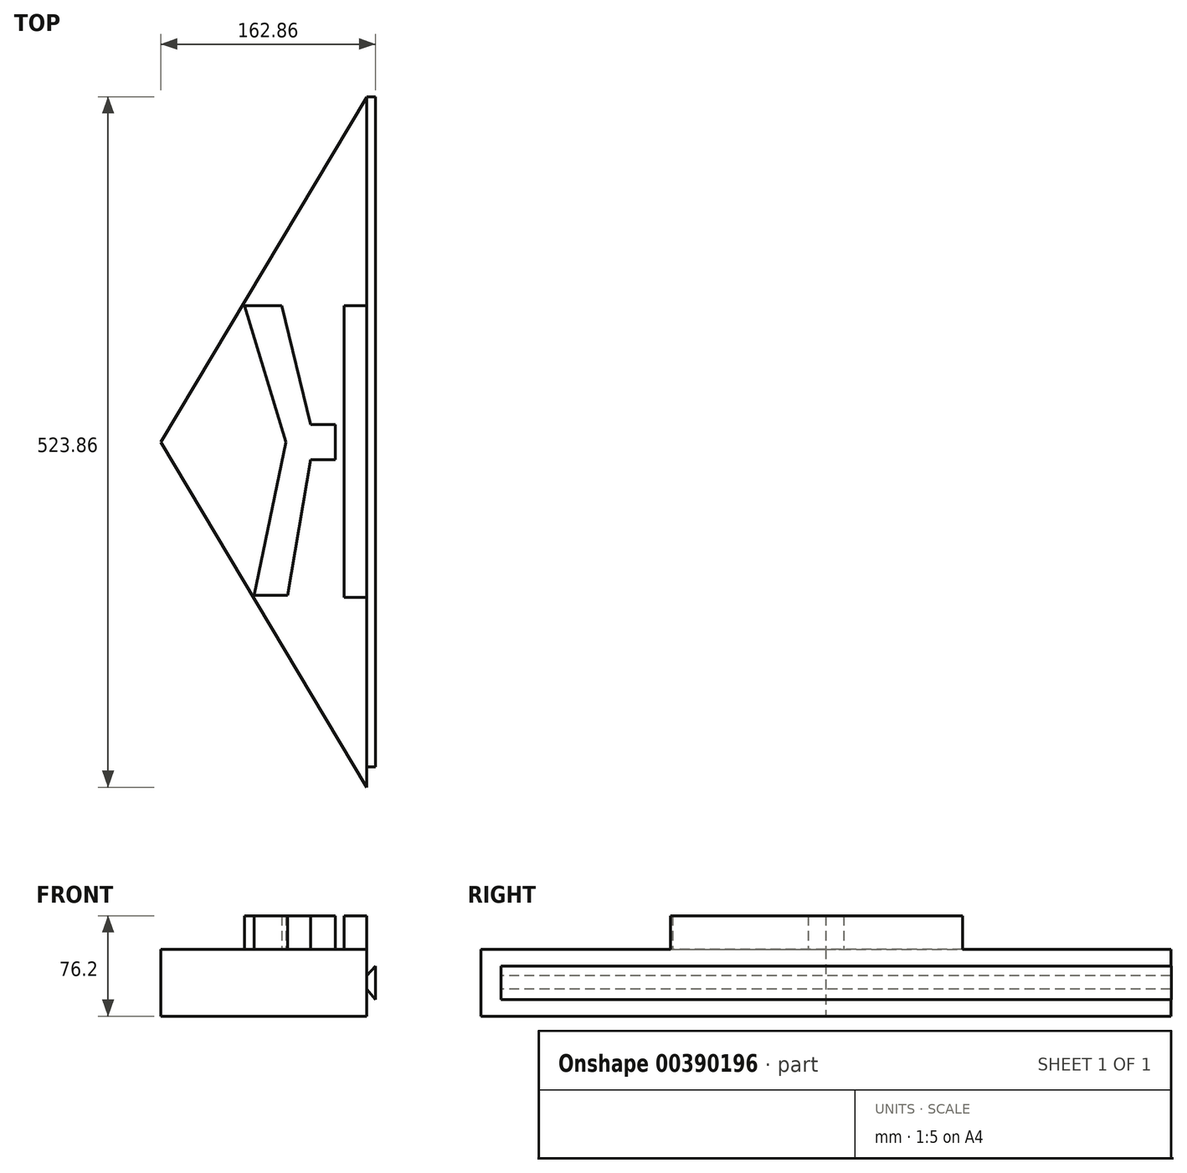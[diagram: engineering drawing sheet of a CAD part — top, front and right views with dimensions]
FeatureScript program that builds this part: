
annotation { "Feature Type Name" : "Feature", "Feature Type Description" : "" }
export const myFeature = defineFeature(function(context is Context, id is Id, definition is map)
    precondition{}
    {
        {
            var Q0;
            Q0=qCreatedBy(makeId("Top.planeOp"),FACE);
            var sketch = newSketch(context, id + "F0", { "sketchPlane" : qUnion([Q0])});
            skLineSegment(sketch, "E0", {"start": v(0, 261.73) * mm, "end": v(0, -261.73) * mm});
            skLineSegment(sketch, "E1", {"start": v(0, -261.73) * mm, "end": v(-156.2, 0) * mm});
            skLineSegment(sketch, "E2", {"start": v(-156.2, 0) * mm, "end": v(0, 261.73) * mm});
            skSolve(sketch);
        }
        {
            var Q0;
            Q0=makeQuery(id+"F0.imprint","IMPRINT",FACE,{"disambiguationData":[TD([[makeQuery(id+"F0.imprint","IMPRINT",EDGE,{"derivedFrom":sQuery(id+"F0.wireOp",EDGE,"E0")}),-1.0]])]});
            extrude(context, id + "F1", {"entities" : qUnion([Q0]), "depth" : 50.8 * mm});
        }
        {
            var Q0;
            Q0=makeQuery(id+"F1.opExtrude","CAP_FACE",FACE,{"disambiguationData":[OSD([sQuery(id+"F0.wireOp",EDGE,"E0"),sQuery(id+"F0.wireOp",EDGE,"E1"),sQuery(id+"F0.wireOp",EDGE,"E2")])],"isStart":false});
            cPlane(context, id + "F2", {"entities" : qUnion([Q0]), "cplaneType" : CPlaneType.OFFSET, "offset" : 0 * mm, "width" : 152.4 * mm, "height" : 152.4 * mm});
        }
        {
            var Q0;
            Q0=qCreatedBy(id+"F2.planeOp",FACE);
            var sketch = newSketch(context, id + "F3", { "sketchPlane" : qUnion([Q0])});
            skLineSegment(sketch, "E3.bottom", {"start": v(0, 103.6) * mm, "end": v(-17.09, 103.6) * mm});
            skLineSegment(sketch, "E3.top", {"start": v(0, -117.89) * mm, "end": v(-17.09, -117.89) * mm});
            skLineSegment(sketch, "E3.left", {"start": v(0, 103.6) * mm, "end": v(0, -117.89) * mm});
            skLineSegment(sketch, "E3.right", {"start": v(-17.09, 103.6) * mm, "end": v(-17.09, -117.89) * mm});
            skLineSegment(sketch, "E4.bottom", {"start": v(-23.86, -13.4) * mm, "end": v(-61.21, -13.4) * mm});
            skLineSegment(sketch, "E4.top", {"start": v(-23.86, 13.4) * mm, "end": v(-61.21, 13.4) * mm});
            skLineSegment(sketch, "E4.left", {"start": v(-23.86, -13.4) * mm, "end": v(-23.86, 13.4) * mm});
            skLineSegment(sketch, "E4.right", {"start": v(-61.21, -13.4) * mm, "end": v(-61.21, 13.4) * mm});
            skPoint(sketch, "E4.middle", {"position": v(-42.54, 0) * mm});
            skLineSegment(sketch, "E5", {"start": v(-61.21, 0) * mm, "end": v(-85.25, -116.21) * mm});
            skLineSegment(sketch, "E6", {"start": v(-85.25, -116.21) * mm, "end": v(-60, -116.21) * mm});
            skLineSegment(sketch, "E7", {"start": v(-60, -116.21) * mm, "end": v(-42.54, -13.4) * mm});
            skLineSegment(sketch, "E8", {"start": v(-61.21, 0) * mm, "end": v(-92.8, 103.65) * mm});
            skLineSegment(sketch, "E9", {"start": v(-92.8, 103.65) * mm, "end": v(-64.5, 103.65) * mm});
            skLineSegment(sketch, "E10", {"start": v(-64.5, 103.65) * mm, "end": v(-42.54, 13.4) * mm});
            skSolve(sketch);
        }
        {
            var Q0;
            Q0 = qSketchRegion(id + "F3", true);
            extrude(context, id + "F4", {"entities" : qUnion([Q0]), "operationType" : NewBodyOperationType.ADD, "depth" : 25.4 * mm});
        }
        {
            var Q0;
            Q0=qCreatedBy(makeId("Front.planeOp"),FACE);
            cPlane(context, id + "F5", {"entities" : qUnion([Q0]), "cplaneType" : CPlaneType.OFFSET, "offset" : 162.56 * mm, "width" : 152.4 * mm, "height" : 152.4 * mm});
        }
        {
            var Q0;
            Q0=qCreatedBy(id+"F5.planeOp",FACE);
            cPlane(context, id + "F6", {"entities" : qUnion([Q0]), "cplaneType" : CPlaneType.OFFSET, "offset" : 83.82 * mm, "width" : 152.4 * mm, "height" : 152.4 * mm});
        }
        {
            var Q0;
            Q0=qCreatedBy(id+"F6.planeOp",FACE);
            var sketch = newSketch(context, id + "F7", { "sketchPlane" : qUnion([Q0])});
            skLineSegment(sketch, "E11", {"start": v(0, 20.42) * mm, "end": v(6.66, 12.72) * mm});
            skLineSegment(sketch, "E12", {"start": v(6.66, 12.72) * mm, "end": v(6.66, 38.05) * mm});
            skLineSegment(sketch, "E13", {"start": v(6.66, 38.05) * mm, "end": v(0, 30.59) * mm});
            skLineSegment(sketch, "E14", {"start": v(0, 30.59) * mm, "end": v(0, 20.42) * mm});
            skSolve(sketch);
        }
        {
            var Q0;
            Q0 = qSketchRegion(id + "F7", true);
            extrude(context, id + "F8", {"entities" : qUnion([Q0]), "operationType" : NewBodyOperationType.ADD, "oppositeDirection" : true, "depth" : 508.5 * mm});
        }
    });
